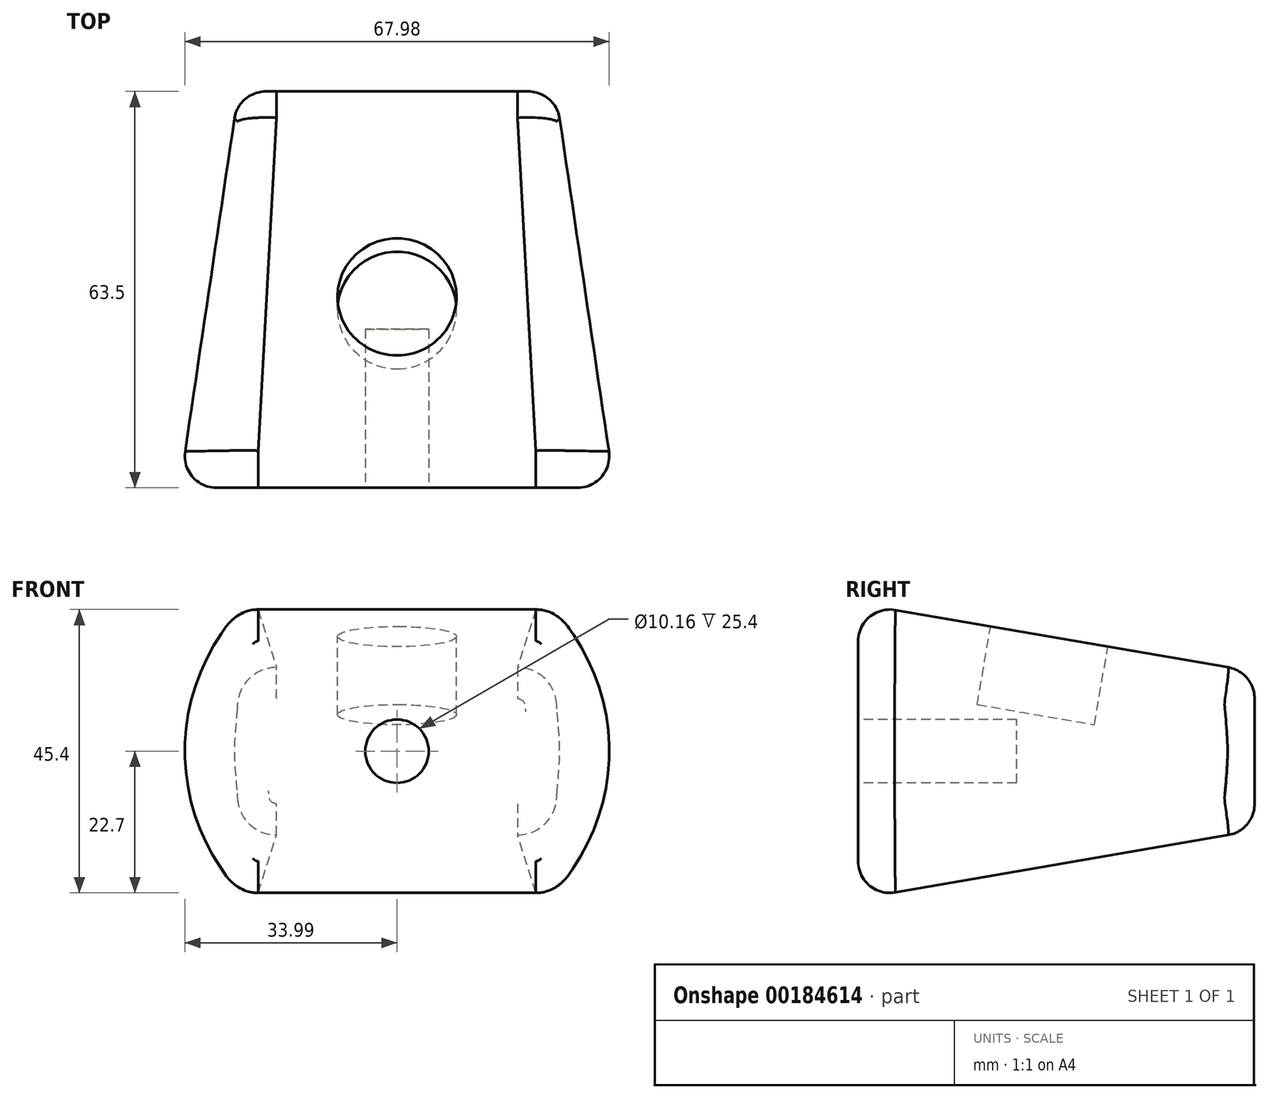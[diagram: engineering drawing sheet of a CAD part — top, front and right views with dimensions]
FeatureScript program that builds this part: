
annotation { "Feature Type Name" : "Feature", "Feature Type Description" : "" }
export const myFeature = defineFeature(function(context is Context, id is Id, definition is map)
    precondition{}
    {
        {
            var Q0;
            Q0=qCreatedBy(makeId("Front.planeOp"),FACE);
            var sketch = newSketch(context, id + "F0", { "sketchPlane" : qUnion([Q0])});
            skLineSegment(sketch, "E0", {"start": v(-59.2, 0) * mm, "end": v(64.6, 0) * mm, "construction": true});
            skPoint(sketch, "E1.visualSharp", {"position": v(-31.75, 39.66) * mm});
            skPoint(sketch, "E2.visualSharp", {"position": v(-31.75, -39.66) * mm});
            skPoint(sketch, "E3.visualSharp", {"position": v(31.75, -39.66) * mm});
            skLineSegment(sketch, "E4.0", {"start": v(-22.58, 23.65) * mm, "end": v(22.58, 23.65) * mm});
            skArc(sketch, "E4.1", {"start": v(-27.62, 21.17) * mm, "mid": v(-34.8, 0) * mm, "end": v(-27.62, -21.17) * mm});
            skLineSegment(sketch, "E4.2", {"start": v(-22.58, -23.65) * mm, "end": v(22.58, -23.65) * mm});
            skArc(sketch, "E4.3", {"start": v(27.62, -21.17) * mm, "mid": v(34.8, 0) * mm, "end": v(27.62, 21.17) * mm});
            skPoint(sketch, "E5.visualSharp", {"position": v(25.52, 23.65) * mm});
            skArc(sketch, "E5.filletArc", {"start": v(27.62, 21.17) * mm, "mid": v(25.4, 23) * mm, "end": v(22.58, 23.65) * mm});
            skPoint(sketch, "E6.visualSharp", {"position": v(-25.52, 23.65) * mm});
            skArc(sketch, "E6.filletArc", {"start": v(-22.58, 23.65) * mm, "mid": v(-25.4, 23) * mm, "end": v(-27.62, 21.17) * mm});
            skPoint(sketch, "E7.visualSharp", {"position": v(-25.52, -23.65) * mm});
            skArc(sketch, "E7.filletArc", {"start": v(-27.62, -21.17) * mm, "mid": v(-25.4, -23) * mm, "end": v(-22.58, -23.65) * mm});
            skPoint(sketch, "E8.visualSharp", {"position": v(25.52, -23.65) * mm});
            skArc(sketch, "E8.filletArc", {"start": v(22.58, -23.65) * mm, "mid": v(25.4, -23) * mm, "end": v(27.62, -21.17) * mm});
            skSolve(sketch);
        }
        {
            var Q0;
            Q0=qCreatedBy(makeId("Front.planeOp"),FACE);
            cPlane(context, id + "F1", {"entities" : qUnion([Q0]), "cplaneType" : CPlaneType.OFFSET, "offset" : 63.5 * mm, "oppositeDirection" : true, "width" : 152.4 * mm, "height" : 152.4 * mm});
        }
        {
            var Q0;
            Q0=qCreatedBy(id+"F1.planeOp",FACE);
            var sketch = newSketch(context, id + "F2", { "sketchPlane" : qUnion([Q0])});
            skLineSegment(sketch, "E9.bottom", {"start": v(19.05, -12.7) * mm, "end": v(-19.05, -12.7) * mm});
            skLineSegment(sketch, "E9.top", {"start": v(19.05, 12.7) * mm, "end": v(-19.05, 12.7) * mm});
            skLineSegment(sketch, "E9.left", {"start": v(25.4, -6.35) * mm, "end": v(25.4, 6.35) * mm});
            skLineSegment(sketch, "E9.right", {"start": v(-25.4, -6.35) * mm, "end": v(-25.4, 6.35) * mm});
            skPoint(sketch, "E9.middle", {"position": v(0, 0) * mm});
            skPoint(sketch, "E10.visualSharp", {"position": v(25.4, 12.7) * mm});
            skArc(sketch, "E10.filletArc", {"start": v(25.4, 6.35) * mm, "mid": v(23.54, 10.84) * mm, "end": v(19.05, 12.7) * mm});
            skPoint(sketch, "E11.visualSharp", {"position": v(25.4, -12.7) * mm});
            skArc(sketch, "E11.filletArc", {"start": v(19.05, -12.7) * mm, "mid": v(23.54, -10.84) * mm, "end": v(25.4, -6.35) * mm});
            skPoint(sketch, "E12.visualSharp", {"position": v(-25.4, -12.7) * mm});
            skArc(sketch, "E12.filletArc", {"start": v(-25.4, -6.35) * mm, "mid": v(-23.54, -10.84) * mm, "end": v(-19.05, -12.7) * mm});
            skPoint(sketch, "E13.visualSharp", {"position": v(-25.4, 12.7) * mm});
            skArc(sketch, "E13.filletArc", {"start": v(-19.05, 12.7) * mm, "mid": v(-23.54, 10.84) * mm, "end": v(-25.4, 6.35) * mm});
            skSolve(sketch);
        }
        {
            var Q0;
            Q0=makeQuery(id+"F0.imprint","IMPRINT",FACE,{"disambiguationData":[TD([[makeQuery(id+"F0.imprint","IMPRINT",EDGE,{"derivedFrom":sQuery(id+"F0.wireOp",EDGE,"E4.0")}),-1.0]])]});
            var Q1;
            Q1=makeQuery(id+"F2.imprint","IMPRINT",FACE,{"disambiguationData":[TD([[makeQuery(id+"F2.imprint","IMPRINT",EDGE,{"derivedFrom":sQuery(id+"F2.wireOp",EDGE,"E9.bottom")}),-1.0]])]});
            loft(context, id + "F3", {"sheetProfilesArray" : [{ "sheetProfileEntities" : qUnion([Q0]) }, { "sheetProfileEntities" : qUnion([Q1]) }]});
        }
        {
            var Q0;
            Q0=makeQuery(id+"F3.opLoft","CAP_FACE",FACE,{"disambiguationData":[OSD([makeQuery(id+"F0.imprint","IMPRINT",FACE,{"disambiguationData":[TD([[makeQuery(id+"F0.imprint","IMPRINT",EDGE,{"derivedFrom":sQuery(id+"F0.wireOp",EDGE,"E4.0")}),-1.0]])]})])],"isStart":true});
            var sketch = newSketch(context, id + "F4", { "sketchPlane" : qUnion([Q0])});
            skCircle(sketch, "E14", {"center": v(0, 0) * mm, "radius": 5.08 * mm});
            skSolve(sketch);
        }
        {
            var Q0;
            Q0 = qSketchRegion(id + "F4", true);
            extrude(context, id + "F5", {"entities" : qUnion([Q0]), "operationType" : NewBodyOperationType.REMOVE, "oppositeDirection" : true, "depth" : 25.4 * mm});
        }
        {
            var Q0;
            Q0=makeQuery(id+"F3.opLoft","SWEPT_FACE",FACE,{"disambiguationData":[OSD([sQuery(id+"F0.wireOp",EDGE,"E4.0"),sQuery(id+"F0.wireOp",EDGE,"E5.filletArc"),sQuery(id+"F0.wireOp",EDGE,"E6.filletArc"),sQuery(id+"F2.wireOp",EDGE,"E9.top"),sQuery(id+"F2.wireOp",EDGE,"E10.filletArc"),sQuery(id+"F2.wireOp",EDGE,"E13.filletArc")])]});
            var sketch = newSketch(context, id + "F6", { "sketchPlane" : qUnion([Q0])});
            skCircle(sketch, "E15", {"center": v(0, 27.04) * mm, "radius": 9.53 * mm});
            skSolve(sketch);
        }
        {
            var Q0;
            Q0 = qSketchRegion(id + "F6", true);
            extrude(context, id + "F7", {"entities" : qUnion([Q0]), "operationType" : NewBodyOperationType.REMOVE, "oppositeDirection" : true, "depth" : 12.7 * mm});
        }
        {
            var Q0;
            Q0=makeQuery(id+"F5.boolean.opBoolean","COPY",EDGE,{"derivedFrom":makeQuery(id+"F5.opExtrude","CAP_EDGE",EDGE,{"disambiguationData":[OSD([sQuery(id+"F4.wireOp",EDGE,"E14")])],"isStart":true})});
            var Q1;
            Q1=makeQuery(id+"F3.opLoft","MID_CAP_EDGE",EDGE,{"disambiguationData":[OSD([sQuery(id+"F0.wireOp",EDGE,"E4.1"),sQuery(id+"F0.wireOp",EDGE,"E6.filletArc"),sQuery(id+"F0.wireOp",EDGE,"E7.filletArc")])],"capPos":0.0});
            var Q2;
            Q2=makeQuery(id+"F3.opLoft","MID_CAP_EDGE",EDGE,{"disambiguationData":[OSD([sQuery(id+"F2.wireOp",EDGE,"E9.top"),sQuery(id+"F2.wireOp",EDGE,"E10.filletArc"),sQuery(id+"F2.wireOp",EDGE,"E13.filletArc")])],"capPos":1.0});
            var Q3;
            Q3=makeQuery(id+"F3.opLoft","SWEPT_EDGE",EDGE,{"disambiguationData":[OSD([sQuery(id+"F0.wireOp",EDGE,"E4.2"),sQuery(id+"F0.wireOp",EDGE,"E7.filletArc"),sQuery(id+"F2.wireOp",EDGE,"E9.bottom"),sQuery(id+"F2.wireOp",EDGE,"E12.filletArc")])]});
            var Q4;
            Q4=makeQuery(id+"F7.boolean.opBoolean","COPY",EDGE,{"derivedFrom":makeQuery(id+"F7.opExtrude","CAP_EDGE",EDGE,{"disambiguationData":[OSD([sQuery(id+"F6.wireOp",EDGE,"E15")])],"isStart":true})});
            fillet(context, id + "F8", {"entities" : qUnion([Q0, Q1, Q2, Q3, Q4]), "radius" : 5.08 * mm, "tangentPropagation" : true, "allowEdgeOverflow" : false});
        }
    });
